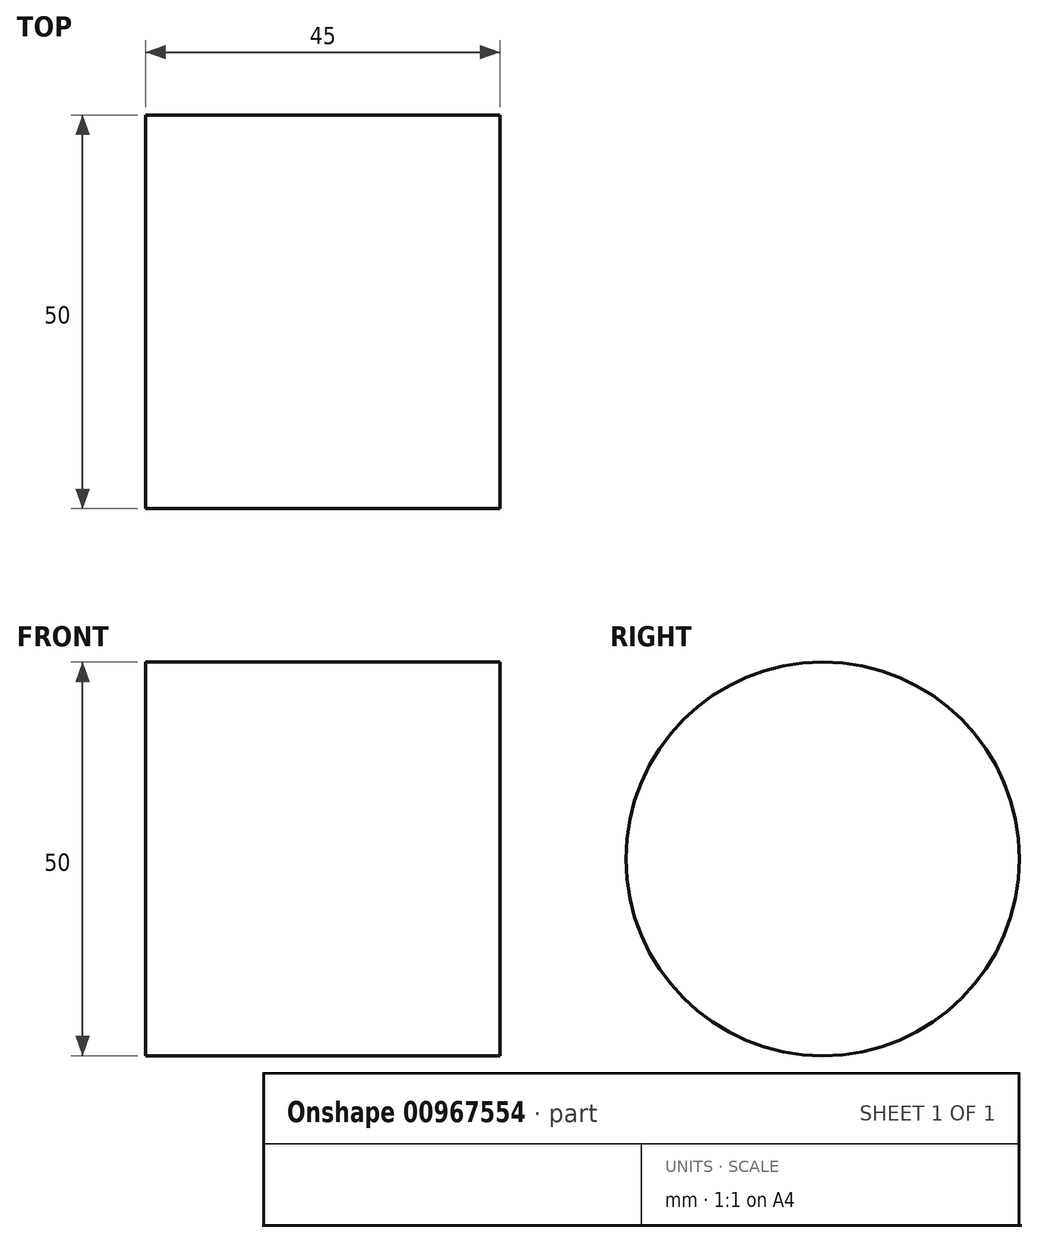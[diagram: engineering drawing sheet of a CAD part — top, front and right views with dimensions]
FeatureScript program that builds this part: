
annotation { "Feature Type Name" : "Feature", "Feature Type Description" : "" }
export const myFeature = defineFeature(function(context is Context, id is Id, definition is map)
    precondition{}
    {
        {
            var Q0;
            Q0=qCreatedBy(makeId("Front.planeOp"),FACE);
            var sketch = newSketch(context, id + "F0", { "sketchPlane" : qUnion([Q0])});
            skLineSegment(sketch, "E0", {"start": v(0, 0) * mm, "end": v(45, 0) * mm});
            skLineSegment(sketch, "E1", {"start": v(45, 0) * mm, "end": v(45, 25) * mm});
            skLineSegment(sketch, "E2", {"start": v(45, 25) * mm, "end": v(0, 25) * mm});
            skLineSegment(sketch, "E3", {"start": v(0, 25) * mm, "end": v(0, 0) * mm});
            skSolve(sketch);
        }
        {
            var Q0;
            Q0=makeQuery(id+"F0.imprint","IMPRINT",FACE,{"disambiguationData":[TD([[makeQuery(id+"F0.imprint","IMPRINT",EDGE,{"derivedFrom":sQuery(id+"F0.wireOp",EDGE,"E0")}),1.0]])]});
            var Q1;
            Q1=sQuery(id+"F0.wireOp",EDGE,"E2");
            revolve(context, id + "F1", {"surfaceOperationType" : NewSurfaceOperationType.NEW, "entities" : qUnion([Q0]), "axis" : qUnion([Q1]), "revolveType" : RevolveType.FULL});
        }
    });
